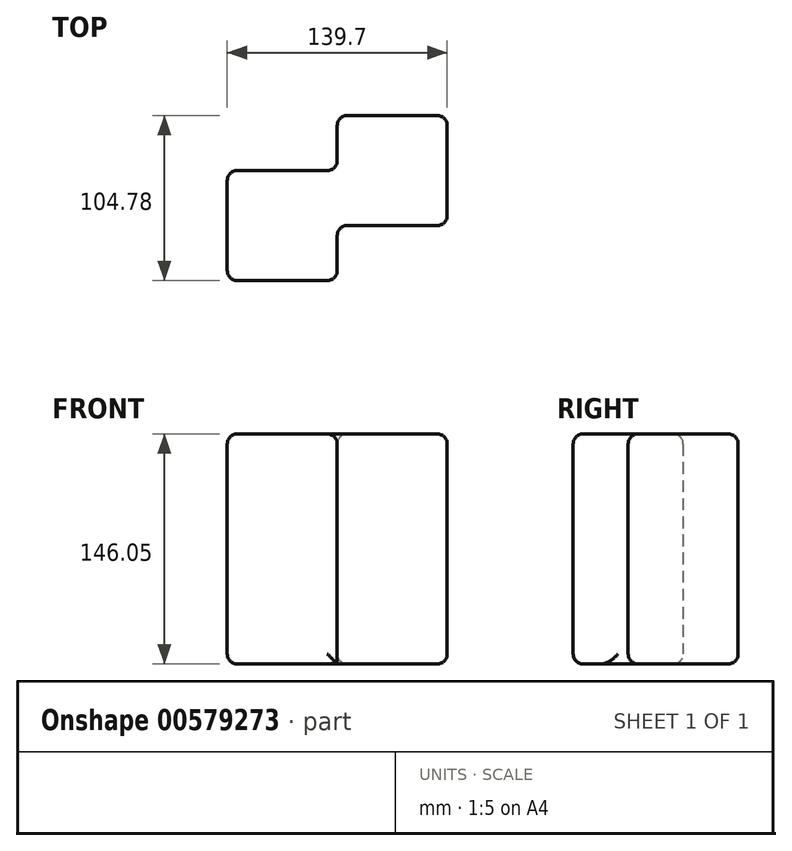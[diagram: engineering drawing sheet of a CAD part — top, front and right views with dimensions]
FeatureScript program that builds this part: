
annotation { "Feature Type Name" : "Feature", "Feature Type Description" : "" }
export const myFeature = defineFeature(function(context is Context, id is Id, definition is map)
    precondition{}
    {
        {
            var Q0;
            Q0=qCreatedBy(makeId("Top.planeOp"),FACE);
            var sketch = newSketch(context, id + "F0", { "sketchPlane" : qUnion([Q0])});
            skLineSegment(sketch, "E0.bottom", {"start": v(0, -17.46) * mm, "end": v(69.85, -17.46) * mm});
            skLineSegment(sketch, "E0.top", {"start": v(0, 52.39) * mm, "end": v(69.85, 52.39) * mm});
            skLineSegment(sketch, "E0.left", {"start": v(0, 17.46) * mm, "end": v(0, 52.39) * mm});
            skLineSegment(sketch, "E0.right", {"start": v(69.85, -17.46) * mm, "end": v(69.85, 52.39) * mm});
            skLineSegment(sketch, "E1.bottom", {"start": v(0, 17.46) * mm, "end": v(-69.85, 17.46) * mm});
            skLineSegment(sketch, "E1.top", {"start": v(0, -52.39) * mm, "end": v(-69.85, -52.39) * mm});
            skLineSegment(sketch, "E1.left", {"start": v(0, -17.46) * mm, "end": v(0, -52.39) * mm});
            skLineSegment(sketch, "E1.right", {"start": v(-69.85, 17.46) * mm, "end": v(-69.85, -52.39) * mm});
            skSolve(sketch);
        }
        {
            var Q0;
            Q0 = qSketchRegion(id + "F0", true);
            extrude(context, id + "F1", {"entities" : qUnion([Q0]), "depth" : 146.05 * mm, "offsetDistance" : 25.4 * mm});
        }
        {
            var Q0;
            Q0=makeQuery(id+"F1.opExtrude","CAP_FACE",FACE,{"disambiguationData":[OSD([sQuery(id+"F0.wireOp",EDGE,"E0.bottom"),sQuery(id+"F0.wireOp",EDGE,"E0.top"),sQuery(id+"F0.wireOp",EDGE,"E0.left"),sQuery(id+"F0.wireOp",EDGE,"E0.right"),sQuery(id+"F0.wireOp",EDGE,"E1.bottom"),sQuery(id+"F0.wireOp",EDGE,"E1.top"),sQuery(id+"F0.wireOp",EDGE,"E1.left"),sQuery(id+"F0.wireOp",EDGE,"E1.right")])],"isStart":false});
            var Q1;
            Q1=makeQuery(id+"F1.opExtrude","SWEPT_FACE",FACE,{"disambiguationData":[OSD([sQuery(id+"F0.wireOp",EDGE,"E1.top")])]});
            var Q2;
            Q2=makeQuery(id+"F1.opExtrude","SWEPT_FACE",FACE,{"disambiguationData":[OSD([sQuery(id+"F0.wireOp",EDGE,"E0.bottom")])]});
            var Q3;
            Q3=makeQuery(id+"F1.opExtrude","SWEPT_FACE",FACE,{"disambiguationData":[OSD([sQuery(id+"F0.wireOp",EDGE,"E0.right")])]});
            var Q4;
            Q4=makeQuery(id+"F1.opExtrude","SWEPT_FACE",FACE,{"disambiguationData":[OSD([sQuery(id+"F0.wireOp",EDGE,"E0.top")])]});
            var Q5;
            Q5=makeQuery(id+"F1.opExtrude","SWEPT_FACE",FACE,{"disambiguationData":[OSD([sQuery(id+"F0.wireOp",EDGE,"E0.left")])]});
            var Q6;
            Q6=makeQuery(id+"F1.opExtrude","SWEPT_FACE",FACE,{"disambiguationData":[OSD([sQuery(id+"F0.wireOp",EDGE,"E1.bottom")])]});
            var Q7;
            Q7=makeQuery(id+"F1.opExtrude","SWEPT_FACE",FACE,{"disambiguationData":[OSD([sQuery(id+"F0.wireOp",EDGE,"E1.right")])]});
            fillet(context, id + "F2", {"entities" : qUnion([Q0, Q1, Q2, Q3, Q4, Q5, Q6, Q7]), "radius" : 6.35 * mm, "tangentPropagation" : true, "allowEdgeOverflow" : false});
        }
    });
